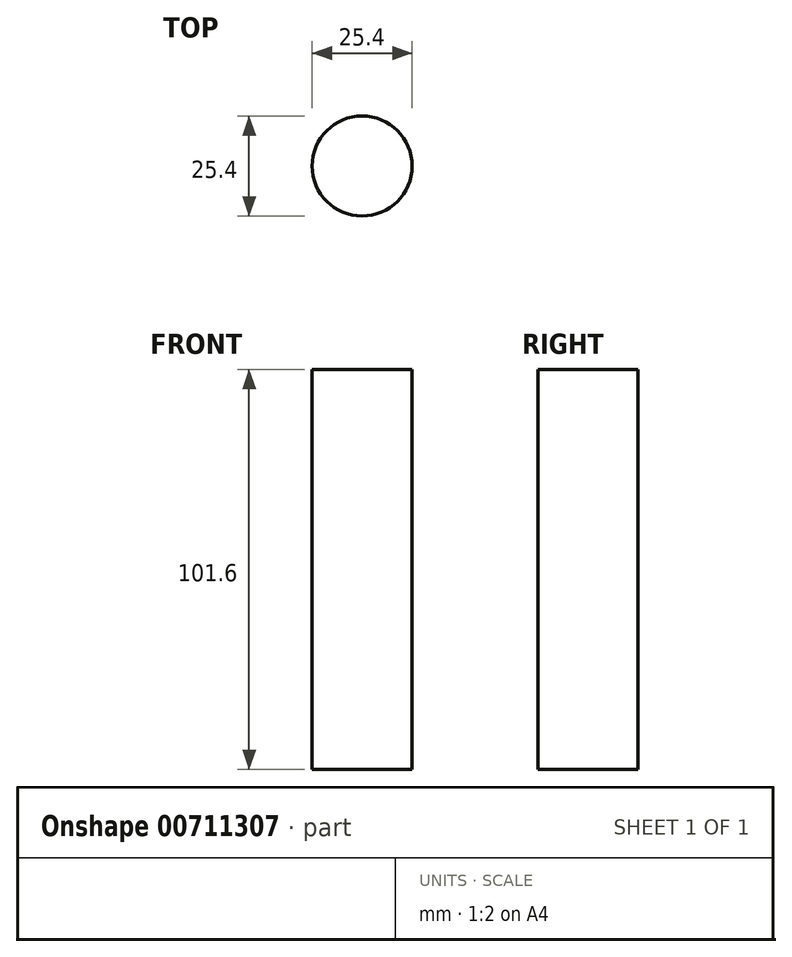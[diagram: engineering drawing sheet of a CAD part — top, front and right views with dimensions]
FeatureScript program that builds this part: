
annotation { "Feature Type Name" : "Feature", "Feature Type Description" : "" }
export const myFeature = defineFeature(function(context is Context, id is Id, definition is map)
    precondition{}
    {
        {
            var Q0;
            Q0=qCreatedBy(makeId("Top.planeOp"),FACE);
            var sketch = newSketch(context, id + "F0", { "sketchPlane" : qUnion([Q0])});
            skCircle(sketch, "E0", {"center": v(0, 0) * mm, "radius": 12.7 * mm});
            skSolve(sketch);
        }
        {
            var Q0;
            Q0=makeQuery(id+"F0.imprint","IMPRINT",FACE,{"disambiguationData":[TD([[makeQuery(id+"F0.imprint","IMPRINT",EDGE,{"derivedFrom":sQuery(id+"F0.wireOp",EDGE,"E0")}),1.0]])]});
            extrude(context, id + "F1", {"entities" : qUnion([Q0]), "depth" : 101.6 * mm, "offsetDistance" : 25.4 * mm});
        }
    });
